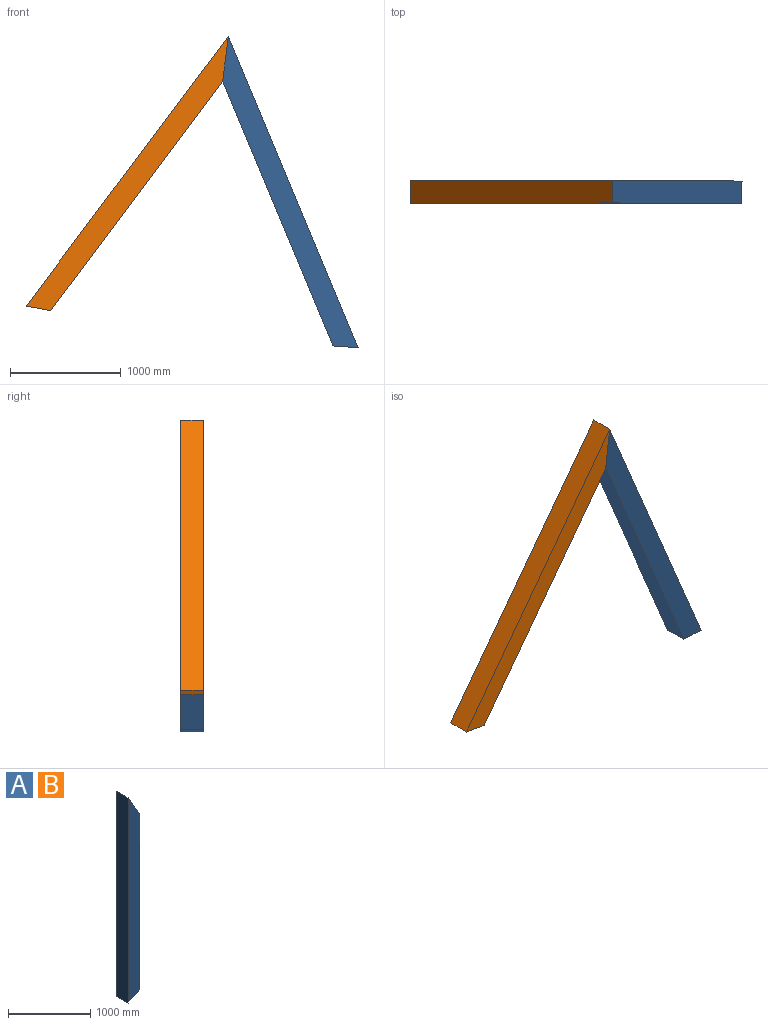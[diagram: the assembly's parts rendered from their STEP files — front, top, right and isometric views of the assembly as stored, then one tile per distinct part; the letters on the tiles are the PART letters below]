
ASSEMBLY  parts=2 mates=1
PART A: 6 faces, bbox 203.2x203.2x3048 mm
  f0: plane 3048x203.2mm, normal (0,-1,0), area 572902.1mm2, adj f1,f3,f4,f5
  f1: plane 2590.8x203.2mm, normal (1,0,0), area 526450.6mm2, adj f0,f2,f4,f5
  f2: plane 3048x203.2mm, normal (0,1,0), area 572902.1mm2, adj f1,f3,f4,f5
  f3: plane 3048x203.2mm, normal (-1,0,0), area 619353.6mm2, adj f0,f2,f4,f5
  f4: plane 203.2x203.2mm, normal (0.45,0,-0.89), area 46163.9mm2, adj f0,f1,f2,f3
  f5: plane 355.6x203.2mm, normal (0.87,0,0.5), area 83223.1mm2, adj f0,f1,f2,f3
PART B: same geometry as A
PLACE A rot(axis=(-0.2,0,0.98),180deg) t=(2798.72,251.99,233.01)mm
PLACE B rot(axis=(0,1,0),36.9deg) t=(-202.39,48.79,608.15)mm
MATE fastened B.f5 <-> A.f5  axis (0.99,0,-0.12) through (1601.01,150.39,2843.35)mm
